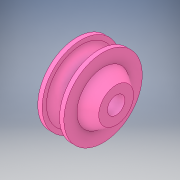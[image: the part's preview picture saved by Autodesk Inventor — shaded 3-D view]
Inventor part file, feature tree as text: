
AUTODESK INVENTOR PART (.ipt)
format: ipt  version: 2017 SP1 (Build 210196100, 196)  size: 182,272 bytes
history: native  units: in
note: dims shown in document units (in); Inventor stores cm internally (conversion verified against a paired STEP export)
features: sketch x2, revolve x1, extrude x1
ambient origin geometry x8: Origin, YZ Plane, XZ Plane, XY Plane, X Axis, Y Axis, Z Axis, Center Point
bodies: Solid1 (feature_tree)
feature tree (4):
  revolve  "Revolution1"  [1 undecoded]
  extrude  "Extrusion1"  Depth=0.125in
  sketch  "Sketch1"  dims[d1=0.0625in d2=0.0625in]
  sketch  "Sketch2"  dims[d7=0.375in d8=0.125in d10=0.125in d11=0.375in d12=0.75in d13=0.125in d14=0.125in d15=90.0deg d16=0.625in d17=0.25in d18=0.0in]
note: 1 required parameter value undecoded (feature->parameter linkage not recoverable at this tier; creation-order binding heuristic only, values carry confidence <= 0.55)
